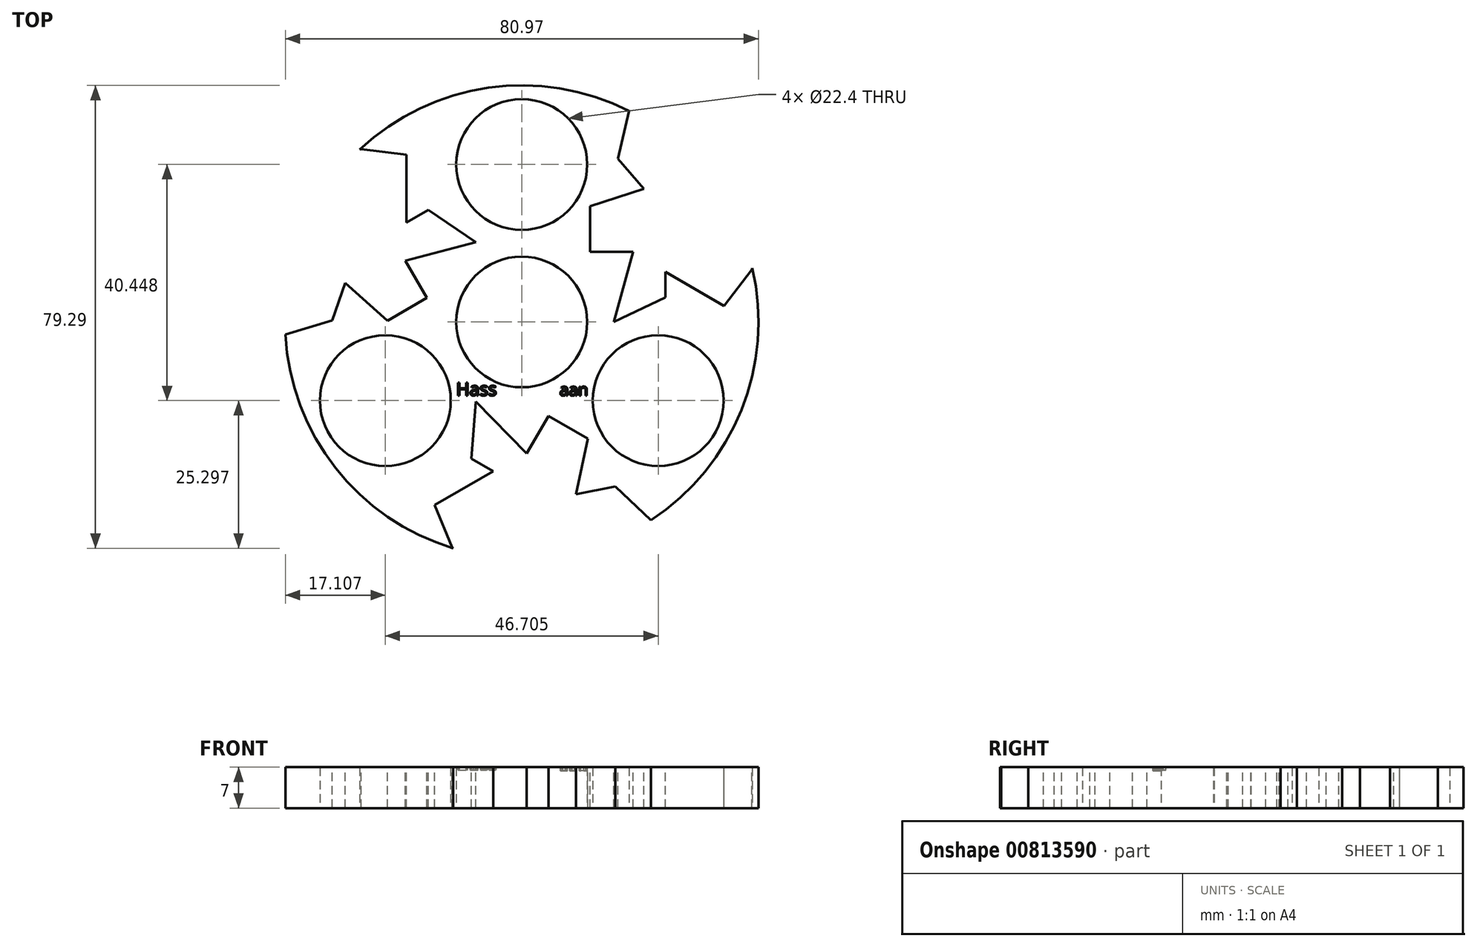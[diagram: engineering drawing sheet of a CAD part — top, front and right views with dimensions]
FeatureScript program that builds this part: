
annotation { "Feature Type Name" : "Feature", "Feature Type Description" : "" }
export const myFeature = defineFeature(function(context is Context, id is Id, definition is map)
    precondition{}
    {
        {
            var Q0;
            Q0=qCreatedBy(makeId("Top.planeOp"),FACE);
            var sketch = newSketch(context, id + "F0", { "sketchPlane" : qUnion([Q0])});
            skCircle(sketch, "E0", {"center": v(0, 0) * mm, "radius": 11.2 * mm});
            skCircle(sketch, "E1", {"center": v(0, 26.97) * mm, "radius": 11.2 * mm});
            skCircle(sketch, "E2.1.1", {"center": v(-23.35, -13.48) * mm, "radius": 11.2 * mm});
            skCircle(sketch, "E2.2.1", {"center": v(23.35, -13.48) * mm, "radius": 11.2 * mm});
            skPoint(sketch, "E3.endSnap0", {"position": v(0.07, 40.17) * mm});
            skCircle(sketch, "E4", {"center": v(0, 0) * mm, "radius": 40.51 * mm});
            skSolve(sketch);
        }
        {
            var Q0;
            Q0=makeQuery(id+"F0.imprint","IMPRINT",FACE,{"disambiguationData":[TD([[makeQuery(id+"F0.imprint","IMPRINT",EDGE,{"derivedFrom":sQuery(id+"F0.wireOp",EDGE,"E0")}),-1.0]])]});
            extrude(context, id + "F1", {"entities" : qUnion([Q0]), "depth" : 7 * mm, "offsetDistance" : 25 * mm});
        }
        {
            var Q0;
            Q0=makeQuery(id+"F1.opExtrude","CAP_FACE",FACE,{"disambiguationData":[OSD([sQuery(id+"F0.wireOp",EDGE,"E0"),sQuery(id+"F0.wireOp",EDGE,"iOuj9urM-kPWP-TESm-DFNk-QvTpCBPu9pPp"),sQuery(id+"F0.wireOp",EDGE,"E1"),sQuery(id+"F0.wireOp",EDGE,"E2.1.0"),sQuery(id+"F0.wireOp",EDGE,"E2.1.1"),sQuery(id+"F0.wireOp",EDGE,"E2.2.0"),sQuery(id+"F0.wireOp",EDGE,"E2.2.1"),sQuery(id+"F0.wireOp",EDGE,"9zKHMhYr-QlHV-07D5-TOaF-jFMu9e6CvLX4"),sQuery(id+"F0.wireOp",EDGE,"83ddaa59-6731-409f-8baf-a3f3c2719c7b.1.0"),sQuery(id+"F0.wireOp",EDGE,"83ddaa59-6731-409f-8baf-a3f3c2719c7b.2.0")])],"isStart":false});
            var sketch = newSketch(context, id + "F2", { "sketchPlane" : qUnion([Q0])});
            skText(sketch, "E5", { "text": "Hass", "fontName": "OpenSans-Regular.ttf"});
            const initialGuessF2  = {"E5": [-0.01121, -0.0126, 1, 0, 0.00222]};
            skSetInitialGuess(sketch, initialGuessF2);
            skSolve(sketch);
        }
        {
            var Q0;
            Q0=qSketchRegion(id+"F2",true);
            extrude(context, id + "F3", {"entities" : qUnion([Q0]), "operationType" : NewBodyOperationType.REMOVE, "oppositeDirection" : true, "depth" : 0.51 * mm, "offsetDistance" : 25 * mm});
        }
        {
            var Q0;
            {var subQ0=sQuery(id+"F0.wireOp",EDGE,"83ddaa59-6731-409f-8baf-a3f3c2719c7b.1.0");var subQ1=sQuery(id+"F0.wireOp",EDGE,"9zKHMhYr-QlHV-07D5-TOaF-jFMu9e6CvLX4");var subQ2=sQuery(id+"F0.wireOp",EDGE,"E2.2.1");var subQ3=sQuery(id+"F0.wireOp",EDGE,"E2.2.0");var subQ4=sQuery(id+"F0.wireOp",EDGE,"E2.1.1");var subQ5=sQuery(id+"F0.wireOp",EDGE,"83ddaa59-6731-409f-8baf-a3f3c2719c7b.2.0");var subQ6=sQuery(id+"F0.wireOp",EDGE,"E0");var subQ7=sQuery(id+"F0.wireOp",EDGE,"E2.1.0");var subQ8=sQuery(id+"F0.wireOp",EDGE,"iOuj9urM-kPWP-TESm-DFNk-QvTpCBPu9pPp");var subQ9=sQuery(id+"F0.wireOp",EDGE,"E1");Q0=makeQuery(id+"F3.boolean.opBoolean","SPLIT",FACE,{"disambiguationData":[TD([makeQuery(id+"F1.opExtrude","SWEPT_FACE",FACE,{"disambiguationData":[OSD([subQ6])]})])],"derivedFrom":makeQuery(id+"F1.opExtrude","CAP_FACE",FACE,{"disambiguationData":[OSD([subQ6,subQ8,subQ9,subQ7,subQ4,subQ3,subQ2,subQ1,subQ0,subQ5])],"isStart":false})});}
            var sketch = newSketch(context, id + "F4", { "sketchPlane" : qUnion([Q0])});
            skText(sketch, "E6", { "text": "aan", "fontName": "OpenSans-Regular.ttf"});
            const initialGuessF4  = {"E6": [0.00646, -0.01262, 1, 0, 0.00205]};
            skSetInitialGuess(sketch, initialGuessF4);
            skSolve(sketch);
        }
        {
            var Q0;
            Q0=qSketchRegion(id+"F4",true);
            extrude(context, id + "F5", {"entities" : qUnion([Q0]), "operationType" : NewBodyOperationType.REMOVE, "oppositeDirection" : true, "depth" : 0.64 * mm, "offsetDistance" : 25 * mm});
        }
        {
            var Q0;
            {var subQ43=sQuery(id+"F0.wireOp",EDGE,"83ddaa59-6731-409f-8baf-a3f3c2719c7b.2.0");var subQ47=sQuery(id+"F0.wireOp",EDGE,"83ddaa59-6731-409f-8baf-a3f3c2719c7b.1.0");var subQ51=sQuery(id+"F0.wireOp",EDGE,"9zKHMhYr-QlHV-07D5-TOaF-jFMu9e6CvLX4");var subQ55=sQuery(id+"F0.wireOp",EDGE,"E2.2.1");var subQ59=sQuery(id+"F0.wireOp",EDGE,"E2.1.1");var subQ62=sQuery(id+"F0.wireOp",EDGE,"E1");var subQ66=sQuery(id+"F0.wireOp",EDGE,"iOuj9urM-kPWP-TESm-DFNk-QvTpCBPu9pPp");var subQ70=sQuery(id+"F0.wireOp",EDGE,"E2.1.0");var subQ75=sQuery(id+"F0.wireOp",EDGE,"E0");var subQ76=makeQuery(id+"F1.opExtrude","SWEPT_FACE",FACE,{"disambiguationData":[OSD([subQ75])]});var subQ79=sQuery(id+"F0.wireOp",EDGE,"E2.2.0");Q0=makeQuery(id+"F5.boolean.opBoolean","SPLIT",FACE,{"disambiguationData":[TD([subQ76])],"derivedFrom":makeQuery(id+"F3.boolean.opBoolean","SPLIT",FACE,{"disambiguationData":[TD([subQ76])],"derivedFrom":makeQuery(id+"F1.opExtrude","CAP_FACE",FACE,{"disambiguationData":[OSD([subQ75,subQ66,subQ62,subQ70,subQ59,subQ79,subQ55,subQ51,subQ47,subQ43])],"isStart":false})})});}
            var sketch = newSketch(context, id + "F6", { "sketchPlane" : qUnion([Q0])});
            skSolve(sketch);
        }
        {
            var Q0;
            Q0=makeQuery(id+"F6.imprint","IMPRINT",FACE,{"disambiguationData":[TD([[makeQuery(id+"F6.imprint","IMPRINT",EDGE,{"derivedFrom":makeQuery(id+"F1.opExtrude","CAP_EDGE",EDGE,{"disambiguationData":[OSD([sQuery(id+"F0.wireOp",EDGE,"E0")])],"isStart":false})}),-1.0]])]});
            var sketch = newSketch(context, id + "F7", { "sketchPlane" : qUnion([Q0])});
            skLineSegment(sketch, "E7", {"start": v(18.4, 36.28) * mm, "end": v(16.43, 27.97) * mm});
            skLineSegment(sketch, "E8", {"start": v(16.43, 27.97) * mm, "end": v(20.92, 22.82) * mm});
            skLineSegment(sketch, "E9", {"start": v(20.92, 22.82) * mm, "end": v(11.68, 19.79) * mm});
            skLineSegment(sketch, "E10", {"start": v(11.68, 19.79) * mm, "end": v(11.68, 12) * mm});
            skLineSegment(sketch, "E11", {"start": v(11.68, 12) * mm, "end": v(19.07, 12) * mm});
            skLineSegment(sketch, "E12", {"start": v(19.07, 12) * mm, "end": v(15.77, 0) * mm});
            skLineSegment(sketch, "E13", {"start": v(15.77, 0) * mm, "end": v(24.61, 4.22) * mm});
            skLineSegment(sketch, "E14", {"start": v(24.61, 4.22) * mm, "end": v(24.61, 8.57) * mm});
            skLineSegment(sketch, "E15", {"start": v(24.61, 8.57) * mm, "end": v(34.64, 2.77) * mm});
            skLineSegment(sketch, "E16", {"start": v(34.64, 2.77) * mm, "end": v(39.39, 8.97) * mm});
            skLineSegment(sketch, "E17", {"start": v(39.39, 8.97) * mm, "end": v(44.14, 32.32) * mm});
            skLineSegment(sketch, "E18", {"start": v(44.14, 32.32) * mm, "end": v(18.4, 36.28) * mm});
            skLineSegment(sketch, "E19.1.0", {"start": v(-50.06, 22.06) * mm, "end": v(-40.63, -2.2) * mm});
            skLineSegment(sketch, "E19.1.1", {"start": v(-40.63, -2.2) * mm, "end": v(-32.44, 0.24) * mm});
            skLineSegment(sketch, "E19.1.2", {"start": v(-32.44, 0.24) * mm, "end": v(-30.22, 6.7) * mm});
            skLineSegment(sketch, "E19.1.3", {"start": v(-30.22, 6.7) * mm, "end": v(-22.98, 0.22) * mm});
            skLineSegment(sketch, "E19.1.4", {"start": v(-22.98, 0.22) * mm, "end": v(-16.24, 4.11) * mm});
            skLineSegment(sketch, "E19.1.5", {"start": v(-16.24, 4.11) * mm, "end": v(-19.93, 10.51) * mm});
            skLineSegment(sketch, "E19.1.6", {"start": v(-19.93, 10.51) * mm, "end": v(-7.89, 13.66) * mm});
            skLineSegment(sketch, "E19.1.7", {"start": v(-7.89, 13.66) * mm, "end": v(-15.96, 19.2) * mm});
            skLineSegment(sketch, "E19.1.8", {"start": v(-15.96, 19.2) * mm, "end": v(-19.73, 17.03) * mm});
            skLineSegment(sketch, "E19.1.9", {"start": v(-19.73, 17.03) * mm, "end": v(-19.72, 28.62) * mm});
            skLineSegment(sketch, "E19.1.10", {"start": v(-19.72, 28.62) * mm, "end": v(-27.46, 29.63) * mm});
            skLineSegment(sketch, "E19.1.11", {"start": v(-27.46, 29.63) * mm, "end": v(-50.06, 22.06) * mm});
            skLineSegment(sketch, "E19.2.0", {"start": v(5.92, -54.39) * mm, "end": v(22.22, -34.08) * mm});
            skLineSegment(sketch, "E19.2.1", {"start": v(22.22, -34.08) * mm, "end": v(16, -28.21) * mm});
            skLineSegment(sketch, "E19.2.2", {"start": v(16, -28.21) * mm, "end": v(9.3, -29.53) * mm});
            skLineSegment(sketch, "E19.2.3", {"start": v(9.3, -29.53) * mm, "end": v(11.3, -20) * mm});
            skLineSegment(sketch, "E19.2.4", {"start": v(11.3, -20) * mm, "end": v(4.56, -16.12) * mm});
            skLineSegment(sketch, "E19.2.5", {"start": v(4.56, -16.12) * mm, "end": v(0.86, -22.52) * mm});
            skLineSegment(sketch, "E19.2.6", {"start": v(0.86, -22.52) * mm, "end": v(-7.89, -13.66) * mm});
            skLineSegment(sketch, "E19.2.7", {"start": v(-7.89, -13.66) * mm, "end": v(-8.65, -23.42) * mm});
            skLineSegment(sketch, "E19.2.8", {"start": v(-8.65, -23.42) * mm, "end": v(-4.88, -25.6) * mm});
            skLineSegment(sketch, "E19.2.9", {"start": v(-4.88, -25.6) * mm, "end": v(-14.92, -31.38) * mm});
            skLineSegment(sketch, "E19.2.10", {"start": v(-14.92, -31.38) * mm, "end": v(-11.93, -38.6) * mm});
            skLineSegment(sketch, "E19.2.11", {"start": v(-11.93, -38.6) * mm, "end": v(5.92, -54.39) * mm});
            skPoint(sketch, "E19.center", {"position": v(0, 0) * mm});
            skSolve(sketch);
        }
        {
            var Q0;
            Q0 = qSketchRegion(id + "F7", true);
            extrude(context, id + "F8", {"entities" : qUnion([Q0]), "operationType" : NewBodyOperationType.REMOVE, "oppositeDirection" : true, "depth" : 25 * mm, "offsetDistance" : 25 * mm});
        }
    });
